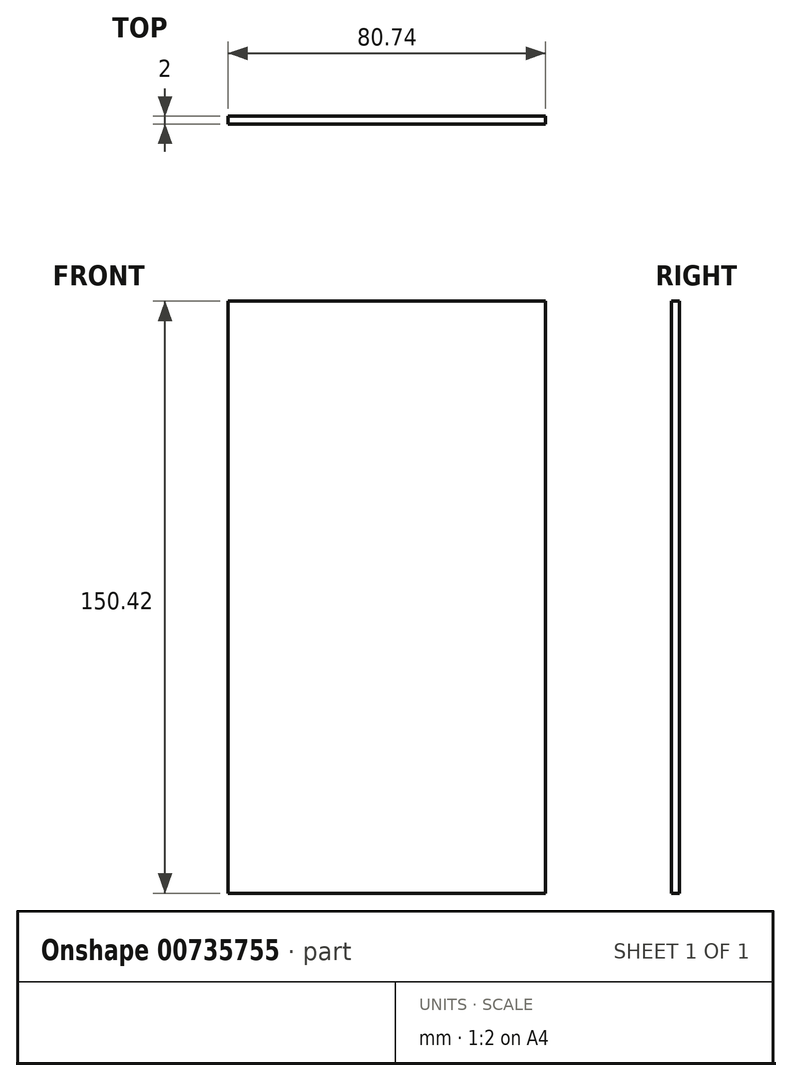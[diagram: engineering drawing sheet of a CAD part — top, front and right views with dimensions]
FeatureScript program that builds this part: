
annotation { "Feature Type Name" : "Feature", "Feature Type Description" : "" }
export const myFeature = defineFeature(function(context is Context, id is Id, definition is map)
    precondition{}
    {
        {
            var Q0;
            Q0=qCreatedBy(makeId("Front.planeOp"),FACE);
            var sketch = newSketch(context, id + "F0", { "sketchPlane" : qUnion([Q0])});
            skLineSegment(sketch, "E0.bottom", {"start": v(40.37, 75.2) * mm, "end": v(-40.37, 75.2) * mm});
            skLineSegment(sketch, "E0.top", {"start": v(40.37, -75.2) * mm, "end": v(-40.37, -75.2) * mm});
            skLineSegment(sketch, "E0.left", {"start": v(40.37, 75.2) * mm, "end": v(40.37, -75.2) * mm});
            skLineSegment(sketch, "E0.right", {"start": v(-40.37, 75.2) * mm, "end": v(-40.37, -75.2) * mm});
            skPoint(sketch, "E0.middle", {"position": v(0, 0) * mm});
            skLineSegment(sketch, "E1.bottom", {"start": v(-40.37, -75.2) * mm, "end": v(40.37, -75.2) * mm});
            skLineSegment(sketch, "E1.top", {"start": v(-40.37, -65.01) * mm, "end": v(40.37, -65.01) * mm});
            skLineSegment(sketch, "E1.left", {"start": v(-40.37, -75.2) * mm, "end": v(-40.37, -65.01) * mm});
            skLineSegment(sketch, "E1.right", {"start": v(40.37, -75.2) * mm, "end": v(40.37, -65.01) * mm});
            skLineSegment(sketch, "E2.top", {"start": v(-40.37, -54.53) * mm, "end": v(40.37, -54.53) * mm});
            skLineSegment(sketch, "E2.left", {"start": v(-40.37, -65.01) * mm, "end": v(-40.37, -54.53) * mm});
            skLineSegment(sketch, "E2.right", {"start": v(40.37, -65.01) * mm, "end": v(40.37, -54.53) * mm});
            skLineSegment(sketch, "E3.bottom", {"start": v(40.37, -54.53) * mm, "end": v(-40.37, -54.53) * mm});
            skLineSegment(sketch, "E3.top", {"start": v(40.37, -43.77) * mm, "end": v(-40.37, -43.77) * mm});
            skLineSegment(sketch, "E3.left", {"start": v(40.37, -54.53) * mm, "end": v(40.37, -43.77) * mm});
            skLineSegment(sketch, "E3.right", {"start": v(-40.37, -54.53) * mm, "end": v(-40.37, -43.77) * mm});
            skLineSegment(sketch, "E4.bottom", {"start": v(-40.37, -43.77) * mm, "end": v(40.37, -43.77) * mm});
            skLineSegment(sketch, "E4.top", {"start": v(-40.37, -33) * mm, "end": v(40.37, -33) * mm});
            skLineSegment(sketch, "E4.left", {"start": v(-40.37, -43.77) * mm, "end": v(-40.37, -33) * mm});
            skLineSegment(sketch, "E4.right", {"start": v(40.37, -43.77) * mm, "end": v(40.37, -33) * mm});
            skLineSegment(sketch, "E5.bottom", {"start": v(40.37, -33) * mm, "end": v(-40.37, -33) * mm});
            skLineSegment(sketch, "E5.top", {"start": v(40.37, -22.24) * mm, "end": v(-40.37, -22.24) * mm});
            skLineSegment(sketch, "E5.left", {"start": v(40.37, -33) * mm, "end": v(40.37, -22.24) * mm});
            skLineSegment(sketch, "E5.right", {"start": v(-40.37, -33) * mm, "end": v(-40.37, -22.24) * mm});
            skLineSegment(sketch, "E6.bottom", {"start": v(-40.37, 75.2) * mm, "end": v(40.37, 75.2) * mm});
            skLineSegment(sketch, "E6.top", {"start": v(-40.37, 64.44) * mm, "end": v(40.37, 64.44) * mm});
            skLineSegment(sketch, "E6.left", {"start": v(-40.37, 75.2) * mm, "end": v(-40.37, 64.44) * mm});
            skLineSegment(sketch, "E6.right", {"start": v(40.37, 75.2) * mm, "end": v(40.37, 64.44) * mm});
            skLineSegment(sketch, "E7.top", {"start": v(-40.37, 53.96) * mm, "end": v(40.37, 53.96) * mm});
            skLineSegment(sketch, "E7.left", {"start": v(-40.37, 64.44) * mm, "end": v(-40.37, 53.96) * mm});
            skLineSegment(sketch, "E7.right", {"start": v(40.37, 64.44) * mm, "end": v(40.37, 53.96) * mm});
            skLineSegment(sketch, "E8.top", {"start": v(-40.37, 43.2) * mm, "end": v(40.37, 43.2) * mm});
            skLineSegment(sketch, "E8.left", {"start": v(-40.37, 53.96) * mm, "end": v(-40.37, 43.2) * mm});
            skLineSegment(sketch, "E8.right", {"start": v(40.37, 53.96) * mm, "end": v(40.37, 43.2) * mm});
            skLineSegment(sketch, "E9.top", {"start": v(-40.37, 32.43) * mm, "end": v(40.37, 32.43) * mm});
            skLineSegment(sketch, "E9.left", {"start": v(-40.37, 43.2) * mm, "end": v(-40.37, 32.43) * mm});
            skLineSegment(sketch, "E9.right", {"start": v(40.37, 43.2) * mm, "end": v(40.37, 32.43) * mm});
            skSolve(sketch);
        }
        {
            var Q0;
            {var subQ0=sQuery(id+"F0.wireOp",EDGE,"E0.bottom");Q0=makeQuery(id+"F0.imprint","IMPRINT",FACE,{"disambiguationData":[TD([[makeQuery(id+"F0.imprint","IMPRINT",EDGE,{"derivedFrom":subQ0}),1.0]])]});}
            var Q1;
            {var subQ0=sQuery(id+"F0.wireOp",EDGE,"E6.top");Q1=makeQuery(id+"F0.imprint","IMPRINT",FACE,{"disambiguationData":[TD([[makeQuery(id+"F0.imprint","IMPRINT",EDGE,{"derivedFrom":subQ0}),-1.0]])]});}
            var Q2;
            {var subQ0=sQuery(id+"F0.wireOp",EDGE,"E7.top");Q2=makeQuery(id+"F0.imprint","IMPRINT",FACE,{"disambiguationData":[TD([[makeQuery(id+"F0.imprint","IMPRINT",EDGE,{"derivedFrom":subQ0}),-1.0]])]});}
            var Q3;
            {var subQ2=sQuery(id+"F0.wireOp",EDGE,"E8.top");Q3=makeQuery(id+"F0.imprint","IMPRINT",FACE,{"disambiguationData":[TD([[makeQuery(id+"F0.imprint","IMPRINT",EDGE,{"derivedFrom":subQ2}),-1.0]])]});}
            extrude(context, id + "F1", {"entities" : qUnion([Q0, Q1, Q2, Q3]), "depth" : 2 * mm, "offsetDistance" : 25 * mm});
        }
        {
            var Q0;
            {var subQ3=sQuery(id+"F0.wireOp",EDGE,"E5.top");var subQ8=makeQuery(id+"F0.imprint","IMPRINT",EDGE,{"derivedFrom":subQ3});var subQ10=sQuery(id+"F0.wireOp",EDGE,"E6.top");var subQ12=sQuery(id+"F0.wireOp",EDGE,"E7.top");var subQ16=makeQuery(id+"F0.imprint","IMPRINT",EDGE,{"derivedFrom":subQ10});var subQ17=makeQuery(id+"F0.imprint","IMPRINT",EDGE,{"derivedFrom":subQ12});var subQ18=sQuery(id+"F0.wireOp",EDGE,"E4.top");var subQ20=makeQuery(id+"F0.imprint","IMPRINT",EDGE,{"derivedFrom":subQ18});var subQ22=sQuery(id+"F0.wireOp",EDGE,"E0.top");var subQ23=sQuery(id+"F0.wireOp",EDGE,"E1.top");var subQ26=makeQuery(id+"F0.imprint","IMPRINT",EDGE,{"derivedFrom":subQ23});var subQ27=sQuery(id+"F0.wireOp",EDGE,"E3.top");var subQ30=makeQuery(id+"F0.imprint","IMPRINT",EDGE,{"derivedFrom":subQ27});var subQ31=sQuery(id+"F0.wireOp",EDGE,"E2.top");var subQ34=makeQuery(id+"F0.imprint","IMPRINT",EDGE,{"derivedFrom":subQ31});var subQ35=sQuery(id+"F0.wireOp",EDGE,"E0.bottom");var subQ36=sQuery(id+"F0.wireOp",EDGE,"E8.top");var subQ39=makeQuery(id+"F0.imprint","IMPRINT",EDGE,{"derivedFrom":subQ36});Q0=qUnion([makeQuery(id+"F0.imprint","IMPRINT",FACE,{"disambiguationData":[TD([[subQ26,1.0]])]}),makeQuery(id+"F0.imprint","IMPRINT",FACE,{"disambiguationData":[TD([[subQ39,-1.0]])]}),makeQuery(id+"F0.imprint","IMPRINT",FACE,{"disambiguationData":[TD([[subQ17,-1.0]])]}),makeQuery(id+"F0.imprint","IMPRINT",FACE,{"disambiguationData":[TD([[makeQuery(id+"F0.imprint","IMPRINT",EDGE,{"derivedFrom":subQ35}),1.0]])]}),makeQuery(id+"F0.imprint","IMPRINT",FACE,{"disambiguationData":[TD([[subQ34,1.0]])]}),makeQuery(id+"F0.imprint","IMPRINT",FACE,{"disambiguationData":[TD([[subQ30,-1.0]])]}),makeQuery(id+"F0.imprint","IMPRINT",FACE,{"disambiguationData":[TD([[makeQuery(id+"F0.imprint","IMPRINT",EDGE,{"derivedFrom":subQ22}),-1.0]])]}),makeQuery(id+"F0.imprint","IMPRINT",FACE,{"disambiguationData":[TD([[subQ20,1.0]])]}),makeQuery(id+"F0.imprint","IMPRINT",FACE,{"disambiguationData":[TD([[subQ16,-1.0]])]}),makeQuery(id+"F0.imprint","IMPRINT",FACE,{"disambiguationData":[TD([[subQ8,-1.0]])]})]);}
            extrude(context, id + "F2", {"entities" : qUnion([Q0]), "operationType" : NewBodyOperationType.ADD, "depth" : 2 * mm, "offsetDistance" : 25 * mm});
        }
    });
